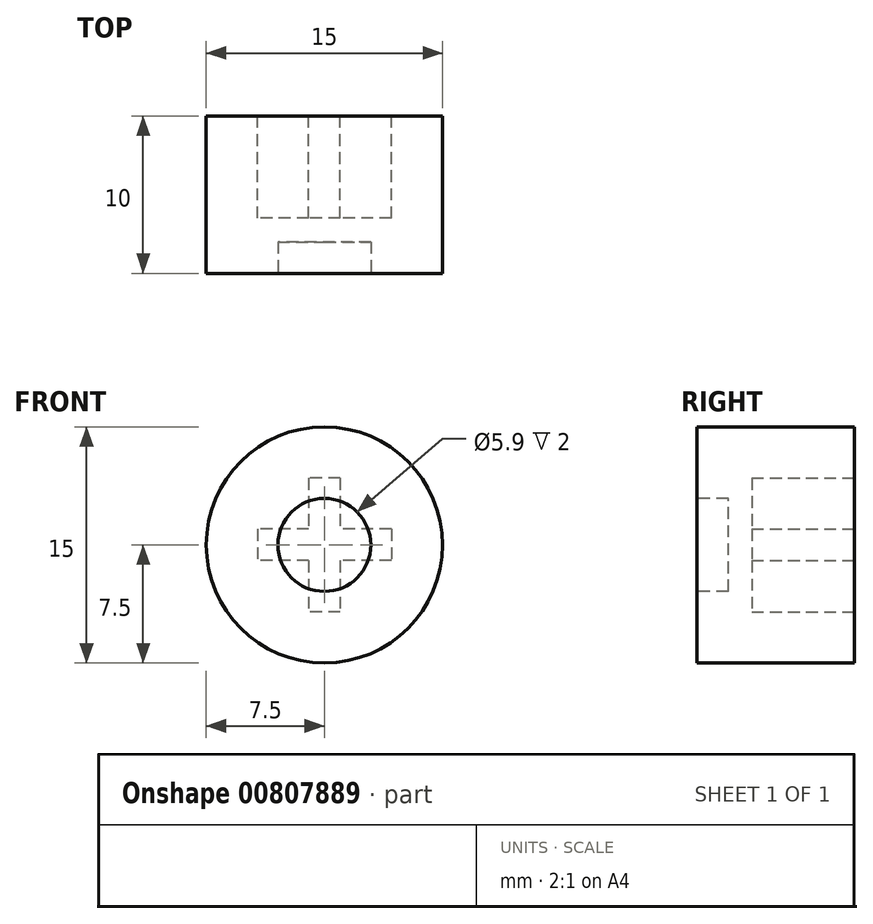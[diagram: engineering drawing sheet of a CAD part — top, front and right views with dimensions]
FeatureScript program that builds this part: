
annotation { "Feature Type Name" : "Feature", "Feature Type Description" : "" }
export const myFeature = defineFeature(function(context is Context, id is Id, definition is map)
    precondition{}
    {
        {
            var Q0;
            Q0=qCreatedBy(makeId("Front.planeOp"),FACE);
            var sketch = newSketch(context, id + "F0", { "sketchPlane" : qUnion([Q0])});
            skCircle(sketch, "E0", {"center": v(0, 0) * mm, "radius": 7.5 * mm});
            skSolve(sketch);
        }
        {
            var Q0;
            Q0 = qSketchRegion(id + "F0", true);
            extrude(context, id + "F1", {"entities" : qUnion([Q0]), "endBound" : BoundingType.SYMMETRIC, "depth" : 10 * mm, "offsetDistance" : 25 * mm});
        }
        {
            var Q0;
            Q0=makeQuery(id+"F1.opExtrude","CAP_FACE",FACE,{"disambiguationData":[OSD([sQuery(id+"F0.wireOp",EDGE,"E0")])],"isStart":false});
            var sketch = newSketch(context, id + "F2", { "sketchPlane" : qUnion([Q0])});
            skCircle(sketch, "E1", {"center": v(0, 0) * mm, "radius": 2.95 * mm});
            skSolve(sketch);
        }
        {
            var Q0;
            Q0=makeQuery(id+"F2.imprint","IMPRINT",FACE,{"disambiguationData":[TD([[makeQuery(id+"F2.imprint","IMPRINT",EDGE,{"derivedFrom":sQuery(id+"F2.wireOp",EDGE,"E1")}),1.0]])]});
            extrude(context, id + "F3", {"entities" : qUnion([Q0]), "operationType" : NewBodyOperationType.REMOVE, "oppositeDirection" : true, "depth" : 2 * mm, "offsetDistance" : 25 * mm});
        }
        {
            var Q0;
            Q0=makeQuery(id+"F1.opExtrude","CAP_FACE",FACE,{"disambiguationData":[OSD([sQuery(id+"F0.wireOp",EDGE,"E0")])],"isStart":true});
            var sketch = newSketch(context, id + "F4", { "sketchPlane" : qUnion([Q0])});
            skLineSegment(sketch, "E2.bottom", {"start": v(-1, 4.25) * mm, "end": v(1, 4.25) * mm});
            skLineSegment(sketch, "E2.top", {"start": v(-1, -4.25) * mm, "end": v(1, -4.25) * mm});
            skLineSegment(sketch, "E2.left", {"start": v(-1, 4.25) * mm, "end": v(-1, 1) * mm});
            skLineSegment(sketch, "E2.right", {"start": v(1, 4.25) * mm, "end": v(1, 1) * mm});
            skLineSegment(sketch, "E3.bottom", {"start": v(-4.25, 1) * mm, "end": v(-1, 1) * mm});
            skLineSegment(sketch, "E3.top", {"start": v(-4.25, -1) * mm, "end": v(-1, -1) * mm});
            skLineSegment(sketch, "E3.left", {"start": v(-4.25, 1) * mm, "end": v(-4.25, -1) * mm});
            skLineSegment(sketch, "E3.right", {"start": v(4.25, 1) * mm, "end": v(4.25, -1) * mm});
            skLineSegment(sketch, "E4.trimOffspring", {"start": v(1, 1) * mm, "end": v(4.25, 1) * mm});
            skLineSegment(sketch, "E5.trimOffspring", {"start": v(-1, -1) * mm, "end": v(-1, -4.25) * mm});
            skLineSegment(sketch, "E6.trimOffspring", {"start": v(1, -1) * mm, "end": v(1, -4.25) * mm});
            skLineSegment(sketch, "E7.trimOffspring", {"start": v(1, -1) * mm, "end": v(4.25, -1) * mm});
            skLineSegment(sketch, "E8", {"start": v(-8.65, 0) * mm, "end": v(10.96, 0) * mm, "construction": true});
            skLineSegment(sketch, "E9", {"start": v(0, 9.35) * mm, "end": v(0, -10.54) * mm, "construction": true});
            skSolve(sketch);
        }
        {
            var Q0;
            Q0=makeQuery(id+"F4.imprint","IMPRINT",FACE,{"disambiguationData":[TD([[makeQuery(id+"F4.imprint","IMPRINT",EDGE,{"derivedFrom":sQuery(id+"F4.wireOp",EDGE,"E2.bottom")}),-1.0]])]});
            extrude(context, id + "F5", {"entities" : qUnion([Q0]), "operationType" : NewBodyOperationType.REMOVE, "oppositeDirection" : true, "depth" : 6.5 * mm, "offsetDistance" : 25 * mm});
        }
    });
